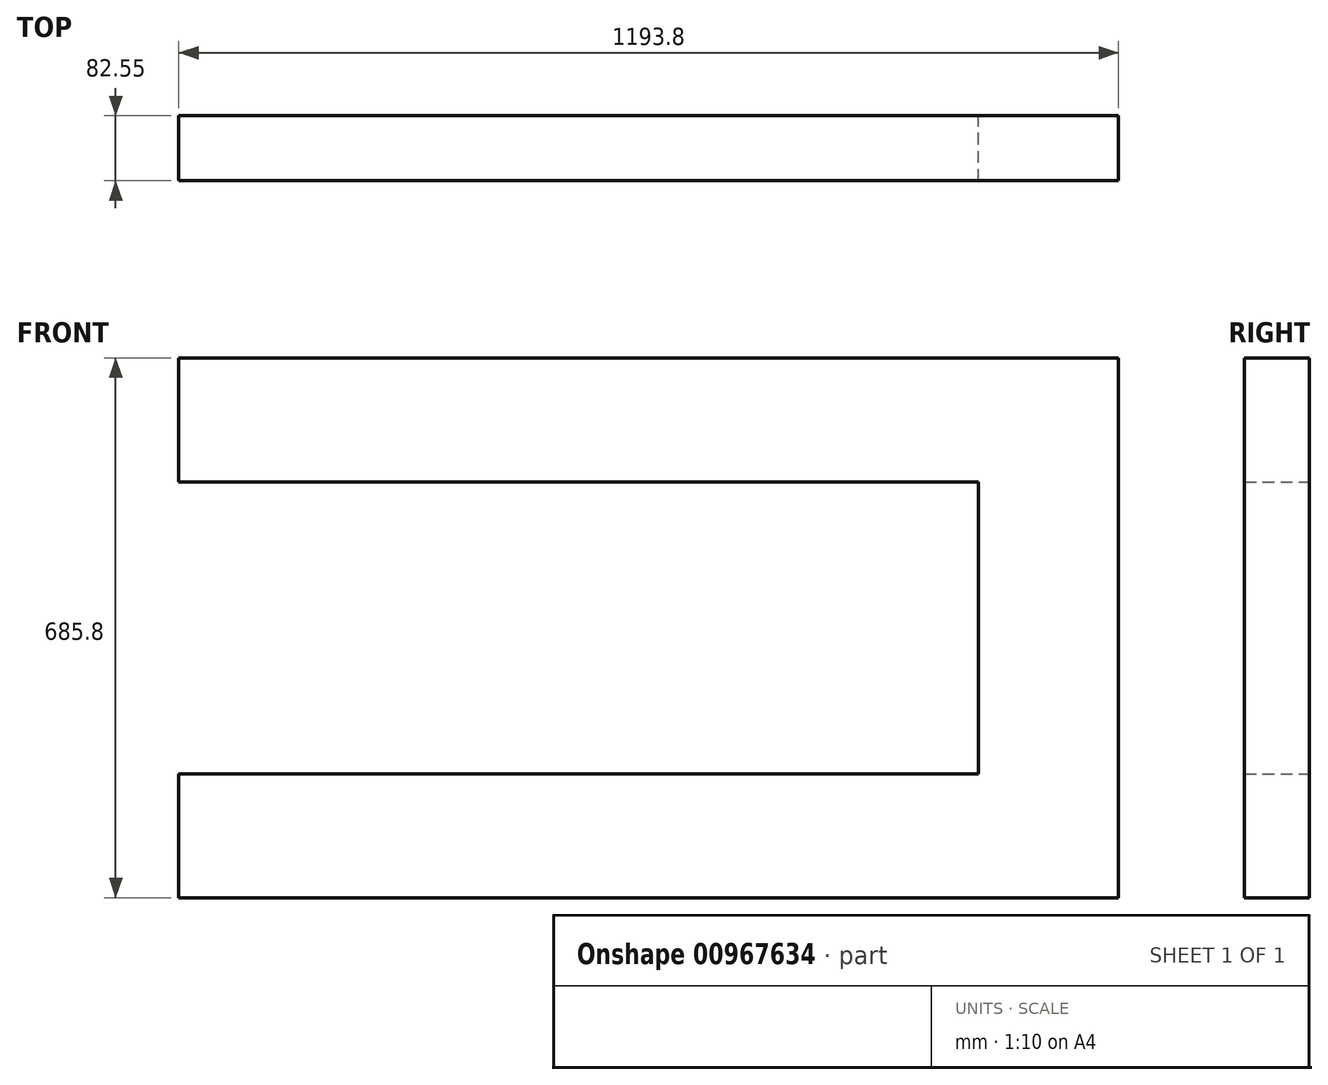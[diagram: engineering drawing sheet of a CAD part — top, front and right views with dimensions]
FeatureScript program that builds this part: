
annotation { "Feature Type Name" : "Feature", "Feature Type Description" : "" }
export const myFeature = defineFeature(function(context is Context, id is Id, definition is map)
    precondition{}
    {
        {
            var Q0;
            Q0=qCreatedBy(makeId("Front.planeOp"),FACE);
            var sketch = newSketch(context, id + "F0", { "sketchPlane" : qUnion([Q0])});
            skLineSegment(sketch, "E0.bottom", {"start": v(0, 0) * mm, "end": v(1193.8, 0) * mm});
            skLineSegment(sketch, "E0.top", {"start": v(0, 685.8) * mm, "end": v(1193.8, 685.8) * mm});
            skLineSegment(sketch, "E0.left", {"start": v(0, 0) * mm, "end": v(0, 685.8) * mm});
            skLineSegment(sketch, "E0.right", {"start": v(1193.8, 0) * mm, "end": v(1193.8, 685.8) * mm});
            skLineSegment(sketch, "E1.bottom", {"start": v(0, 528.32) * mm, "end": v(1016, 528.32) * mm});
            skLineSegment(sketch, "E1.top", {"start": v(0, 157.48) * mm, "end": v(1016, 157.48) * mm});
            skLineSegment(sketch, "E1.left", {"start": v(0, 528.32) * mm, "end": v(0, 157.48) * mm});
            skLineSegment(sketch, "E1.right", {"start": v(1016, 528.32) * mm, "end": v(1016, 157.48) * mm});
            skLineSegment(sketch, "E2", {"start": v(508, 528.32) * mm, "end": v(508, 685.8) * mm, "construction": true});
            skLineSegment(sketch, "E3", {"start": v(508, 157.48) * mm, "end": v(508, 0) * mm, "construction": true});
            skSolve(sketch);
        }
        {
            var Q0;
            {var subQ4=sQuery(id+"F0.wireOp",EDGE,"E0.bottom");Q0=makeQuery(id+"F0.imprint","IMPRINT",FACE,{"disambiguationData":[TD([[makeQuery(id+"F0.imprint","IMPRINT",EDGE,{"derivedFrom":subQ4}),1.0]])]});}
            extrude(context, id + "F1", {"entities" : qUnion([Q0]), "depth" : 82.55 * mm, "offsetDistance" : 25.4 * mm});
        }
    });
